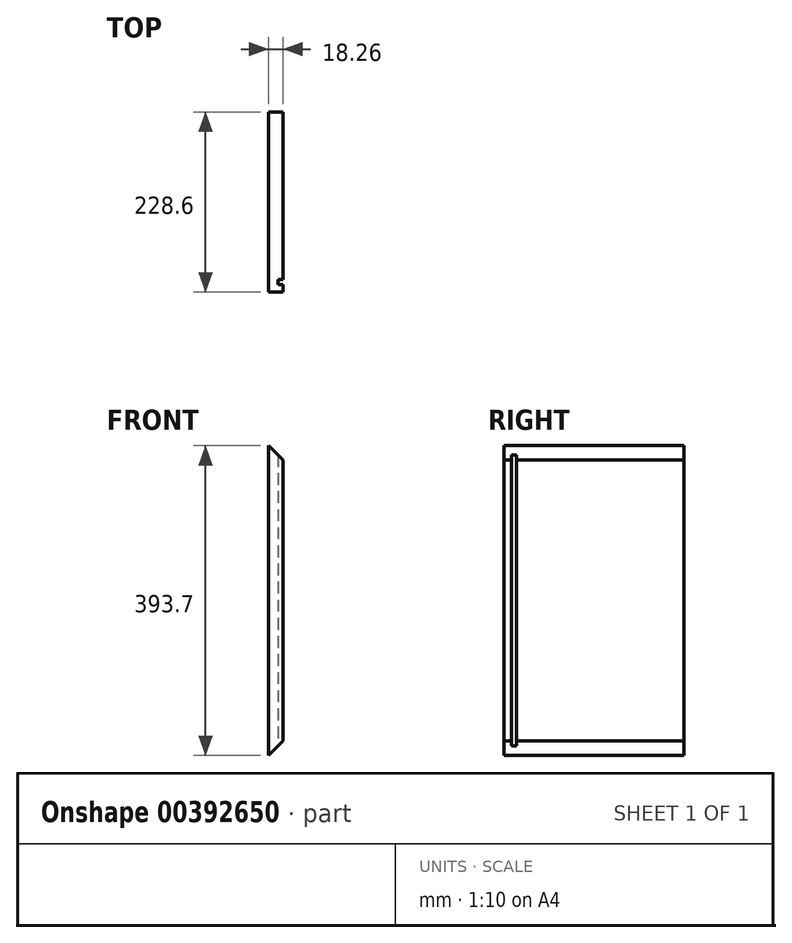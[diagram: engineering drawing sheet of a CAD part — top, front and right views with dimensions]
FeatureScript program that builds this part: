
annotation { "Feature Type Name" : "Feature", "Feature Type Description" : "" }
export const myFeature = defineFeature(function(context is Context, id is Id, definition is map)
    precondition{}
    {
        {
            var Q0;
            Q0=qCreatedBy(makeId("Top.planeOp"),FACE);
            var sketch = newSketch(context, id + "F0", { "sketchPlane" : qUnion([Q0])});
            skLineSegment(sketch, "E0.bottom", {"start": v(9.13, 114.3) * mm, "end": v(-9.13, 114.3) * mm});
            skLineSegment(sketch, "E0.top", {"start": v(9.13, -114.3) * mm, "end": v(-9.13, -114.3) * mm});
            skLineSegment(sketch, "E0.left", {"start": v(9.13, 114.3) * mm, "end": v(9.13, -98.43) * mm});
            skLineSegment(sketch, "E0.right", {"start": v(-9.13, 114.3) * mm, "end": v(-9.13, -114.3) * mm});
            skPoint(sketch, "E0.middle", {"position": v(0, 0) * mm});
            skLineSegment(sketch, "E1.bottom", {"start": v(9.13, -98.43) * mm, "end": v(2.78, -98.43) * mm});
            skLineSegment(sketch, "E1.top", {"start": v(9.13, -104.78) * mm, "end": v(2.78, -104.78) * mm});
            skLineSegment(sketch, "E1.right", {"start": v(2.78, -98.43) * mm, "end": v(2.78, -104.78) * mm});
            skLineSegment(sketch, "E2.trimOffspring", {"start": v(9.13, -104.78) * mm, "end": v(9.13, -114.3) * mm});
            skSolve(sketch);
        }
        {
            var Q0;
            Q0=makeQuery(id+"F0.imprint","IMPRINT",FACE,{"disambiguationData":[TD([[makeQuery(id+"F0.imprint","IMPRINT",EDGE,{"derivedFrom":sQuery(id+"F0.wireOp",EDGE,"E0.bottom")}),1.0]])]});
            extrude(context, id + "F1", {"entities" : qUnion([Q0]), "endBound" : BoundingType.SYMMETRIC, "depth" : 393.7 * mm});
        }
        {
            var Q0;
            Q0=makeQuery(id+"F1.opExtrude","CAP_EDGE",EDGE,{"disambiguationData":[OSD([sQuery(id+"F0.wireOp",EDGE,"E0.left")])],"isStart":false});
            chamfer(context, id + "F2", {"entities" : qUnion([Q0]), "chamferType" : ChamferType.OFFSET_ANGLE, "width" : 18.26 * mm, "oppositeDirection" : false, "angle" : 45 * degree, "tangentPropagation" : true});
        }
        {
            var Q0;
            Q0=makeQuery(id+"F1.opExtrude","CAP_EDGE",EDGE,{"disambiguationData":[OSD([sQuery(id+"F0.wireOp",EDGE,"E0.left")])],"isStart":true});
            chamfer(context, id + "F3", {"entities" : qUnion([Q0]), "width" : 18.26 * mm, "tangentPropagation" : true});
        }
    });
